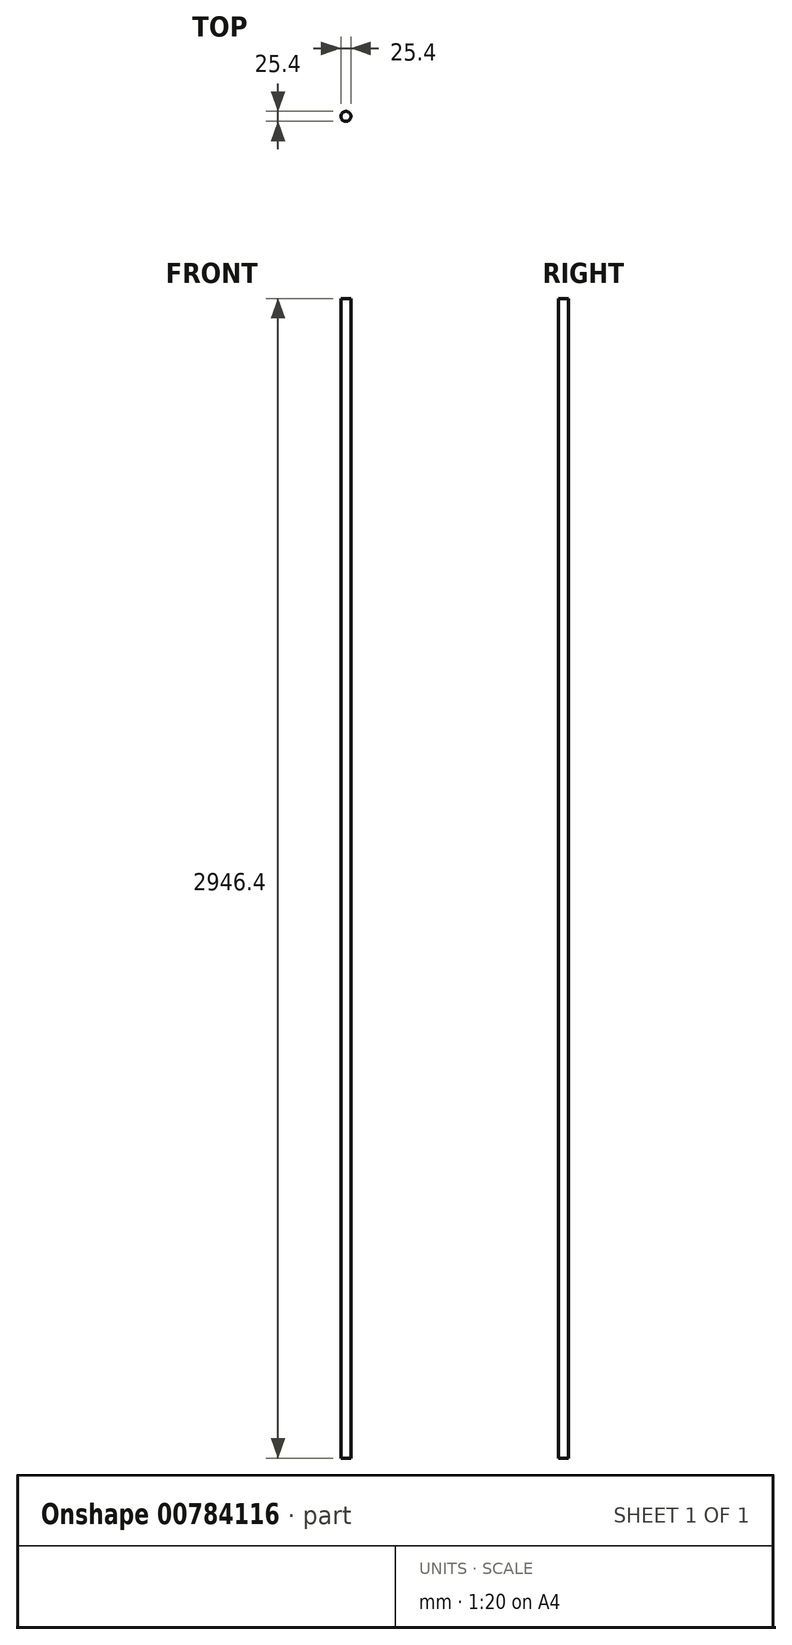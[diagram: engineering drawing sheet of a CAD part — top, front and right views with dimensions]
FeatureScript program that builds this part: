
annotation { "Feature Type Name" : "Feature", "Feature Type Description" : "" }
export const myFeature = defineFeature(function(context is Context, id is Id, definition is map)
    precondition{}
    {
        {
            var Q0;
            Q0=qCreatedBy(makeId("Top.planeOp"),FACE);
            var sketch = newSketch(context, id + "F0", { "sketchPlane" : qUnion([Q0])});
            skCircle(sketch, "E0", {"center": v(0, 0) * mm, "radius": 12.7 * mm});
            skSolve(sketch);
        }
        {
            var Q0;
            Q0 = qSketchRegion(id + "F0", true);
            extrude(context, id + "F1", {"entities" : qUnion([Q0]), "depth" : 2946.4 * mm, "offsetDistance" : 25.4 * mm});
        }
    });
